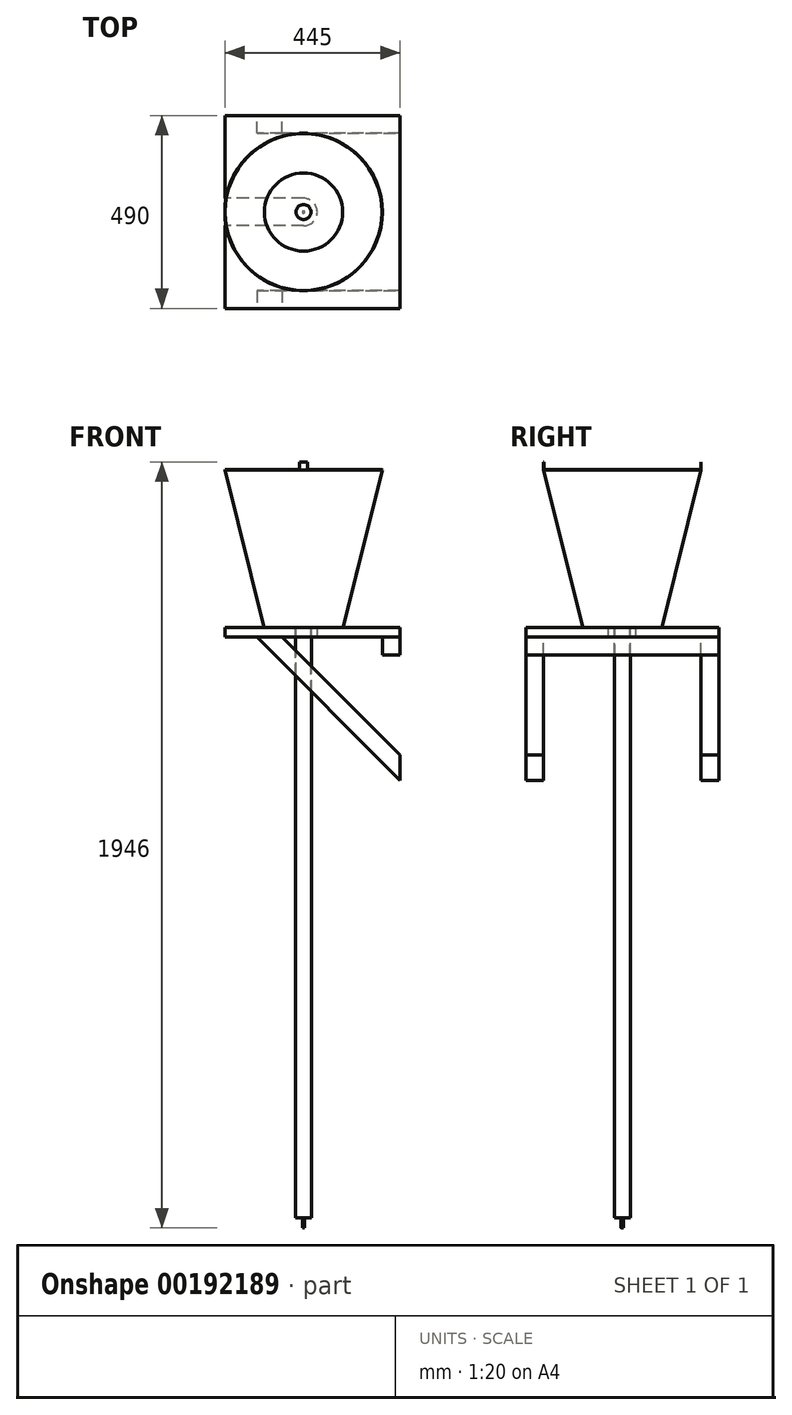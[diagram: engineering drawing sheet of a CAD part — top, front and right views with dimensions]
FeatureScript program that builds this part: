
annotation { "Feature Type Name" : "Feature", "Feature Type Description" : "" }
export const myFeature = defineFeature(function(context is Context, id is Id, definition is map)
    precondition{}
    {
        {
            assignVariable(context, id + "F0", {"name" : "BucketHeight", "anyValue" : 400});
        }
        {
            assignVariable(context, id + "F1", {"name" : "TubeThickness", "anyValue" : 1});
        }
        {
            assignVariable(context, id + "F2", {"name" : "TubeLength", "anyValue" : 1500});
        }
        {
            var Q0;
            Q0=qCreatedBy(makeId("Front.planeOp"),FACE);
            var sketch = newSketch(context, id + "F3", { "sketchPlane" : qUnion([Q0])});
            skLineSegment(sketch, "E0", {"start": v(-29.14, 0) * mm, "end": v(32.36, 0) * mm, "construction": true});
            skLineSegment(sketch, "E1", {"start": v(0, 36.8) * mm, "end": v(0, -14.35) * mm, "construction": true});
            skLineSegment(sketch, "E2", {"start": v(-200, 400) * mm, "end": v(-100, 0) * mm});
            skLineSegment(sketch, "E3", {"start": v(-100, 0) * mm, "end": v(0, 0) * mm});
            skLineSegment(sketch, "E4", {"start": v(0, 0) * mm, "end": v(0, 1) * mm});
            skLineSegment(sketch, "E5", {"start": v(0, 1) * mm, "end": v(-99.22, 1) * mm});
            skLineSegment(sketch, "E6", {"start": v(-99.22, 1) * mm, "end": v(-199.03, 400.24) * mm});
            skLineSegment(sketch, "E7", {"start": v(-199.03, 400.24) * mm, "end": v(-200, 400) * mm});
            skSolve(sketch);
        }
        {
            var Q0;
            Q0 = qSketchRegion(id + "F3", true);
            var Q1;
            Q1=sQuery(id+"F3.wireOp",EDGE,"E1");
            revolve(context, id + "F4", {"entities" : qUnion([Q0]), "axis" : qUnion([Q1]), "revolveType" : RevolveType.FULL});
        }
        {
            var Q0;
            Q0=qCreatedBy(makeId("Top.planeOp"),FACE);
            var sketch = newSketch(context, id + "F5", { "sketchPlane" : qUnion([Q0])});
            skCircle(sketch, "E8", {"center": v(0, 0) * mm, "radius": 20 * mm});
            skCircle(sketch, "E9", {"center": v(0, 0) * mm, "radius": 19 * mm});
            skSolve(sketch);
        }
        {
            var Q0;
            Q0 = qSketchRegion(id + "F5", true);
            extrude(context, id + "F6", {"entities" : qUnion([Q0]), "operationType" : NewBodyOperationType.ADD, "oppositeDirection" : true, "depth" : (getVariable(context, 'TubeLength')) * mm});
        }
        {
            var Q0;
            Q0=qCreatedBy(makeId("Top.planeOp"),FACE);
            var sketch = newSketch(context, id + "F7", { "sketchPlane" : qUnion([Q0])});
            skCircle(sketch, "E10", {"center": v(0, 0) * mm, "radius": 19 * mm});
            skSolve(sketch);
        }
        {
            var Q0;
            Q0 = qSketchRegion(id + "F7", true);
            extrude(context, id + "F8", {"entities" : qUnion([Q0]), "operationType" : NewBodyOperationType.REMOVE, "endBound" : BoundingType.THROUGH_ALL, "depth" : 25 * mm});
        }
        {
            var Q0;
            Q0=qCreatedBy(makeId("Top.planeOp"),FACE);
            cPlane(context, id + "F9", {"entities" : qUnion([Q0]), "cplaneType" : CPlaneType.OFFSET, "offset" : (getVariable(context, 'BucketHeight')) * mm, "width" : 150 * mm, "height" : 150 * mm});
        }
        {
            var Q0;
            Q0=qCreatedBy(id+"F9.planeOp",FACE);
            var sketch = newSketch(context, id + "F10", { "sketchPlane" : qUnion([Q0])});
            skLineSegment(sketch, "E11", {"start": v(0, -264.42) * mm, "end": v(0, 258.28) * mm, "construction": true});
            skLineSegment(sketch, "E12", {"start": v(-81.36, -200) * mm, "end": v(109.19, -200) * mm, "construction": true});
            skLineSegment(sketch, "E13", {"start": v(-77.86, -199.03) * mm, "end": v(90.54, -199.03) * mm, "construction": true});
            skLineSegment(sketch, "E14.bottom", {"start": v(-10, -200) * mm, "end": v(10, -200) * mm});
            skLineSegment(sketch, "E14.top", {"start": v(-10, -199.03) * mm, "end": v(10, -199.03) * mm});
            skLineSegment(sketch, "E14.left", {"start": v(-10, -200) * mm, "end": v(-10, -199.03) * mm});
            skLineSegment(sketch, "E14.right", {"start": v(10, -200) * mm, "end": v(10, -199.03) * mm});
            skLineSegment(sketch, "E15.MirrorCS", {"start": v(-10, 200) * mm, "end": v(-10, 199.03) * mm});
            skLineSegment(sketch, "E16.MirrorCS", {"start": v(10, 200) * mm, "end": v(10, 199.03) * mm});
            skLineSegment(sketch, "E17.MirrorCS", {"start": v(-10, 200) * mm, "end": v(10, 200) * mm});
            skLineSegment(sketch, "E18.MirrorCS", {"start": v(-10, 199.03) * mm, "end": v(10, 199.03) * mm});
            skSolve(sketch);
        }
        {
            var Q0;
            Q0 = qSketchRegion(id + "F10", true);
            extrude(context, id + "F11", {"entities" : qUnion([Q0]), "operationType" : NewBodyOperationType.ADD, "depth" : 20 * mm});
        }
        {
            var Q0;
            Q0=makeQuery(id+"F6.opExtrude","CAP_FACE",FACE,{"disambiguationData":[OSD([sQuery(id+"F5.wireOp",EDGE,"E8"),sQuery(id+"F5.wireOp",EDGE,"E9")])],"isStart":false});
            var sketch = newSketch(context, id + "F12", { "sketchPlane" : qUnion([Q0])});
            skCircle(sketch, "E19", {"center": v(0, 0) * mm, "radius": 20 * mm});
            skSolve(sketch);
        }
        {
            var Q0;
            Q0 = qSketchRegion(id + "F12", true);
            extrude(context, id + "F13", {"entities" : qUnion([Q0]), "operationType" : NewBodyOperationType.ADD, "depth" : (getVariable(context, 'TubeThickness')) * mm});
        }
        {
            var Q0;
            Q0=makeQuery(id+"F13.opExtrude","CAP_FACE",FACE,{"disambiguationData":[OSD([sQuery(id+"F12.wireOp",EDGE,"E19")])],"isStart":false});
            var sketch = newSketch(context, id + "F14", { "sketchPlane" : qUnion([Q0])});
            skCircle(sketch, "E20", {"center": v(0, 0) * mm, "radius": 3 * mm});
            skSolve(sketch);
        }
        {
            var Q0;
            Q0 = qSketchRegion(id + "F14", true);
            extrude(context, id + "F15", {"entities" : qUnion([Q0]), "depth" : 25 * mm});
        }
        {
            var Q0;
            Q0=qCreatedBy(makeId("Top.planeOp"),FACE);
            var sketch = newSketch(context, id + "F16", { "sketchPlane" : qUnion([Q0])});
            skLineSegment(sketch, "E21.bottom", {"start": v(245, -245) * mm, "end": v(-200, -245) * mm});
            skLineSegment(sketch, "E21.top", {"start": v(245, 245) * mm, "end": v(-200, 245) * mm});
            skLineSegment(sketch, "E21.left", {"start": v(245, -245) * mm, "end": v(245, 245) * mm});
            skLineSegment(sketch, "E21.right", {"start": v(-200, -245) * mm, "end": v(-200, -35) * mm});
            skLineSegment(sketch, "E22", {"start": v(347.7, 0) * mm, "end": v(-356.96, 0) * mm, "construction": true});
            skLineSegment(sketch, "E23", {"start": v(0, -400.86) * mm, "end": v(0, 467.96) * mm, "construction": true});
            skArc(sketch, "E24", {"start": v(0, -35) * mm, "mid": v(35, 0) * mm, "end": v(0, 35) * mm});
            skLineSegment(sketch, "E25", {"start": v(0, -35) * mm, "end": v(-200, -35) * mm});
            skLineSegment(sketch, "E26", {"start": v(-200, -35) * mm, "end": v(-191.36, -29) * mm});
            skLineSegment(sketch, "E27", {"start": v(0, 35) * mm, "end": v(-200, 35) * mm});
            skLineSegment(sketch, "E28.trimOffspring", {"start": v(-200, 35) * mm, "end": v(-200, 245) * mm});
            skSolve(sketch);
        }
        {
            var Q0;
            Q0 = qSketchRegion(id + "F16", true);
            extrude(context, id + "F17", {"entities" : qUnion([Q0]), "operationType" : NewBodyOperationType.ADD, "oppositeDirection" : true, "depth" : 25 * mm});
        }
        {
            var Q0;
            Q0=makeQuery(id+"F17.opExtrude","CAP_FACE",FACE,{"disambiguationData":[OSD([sQuery(id+"F16.wireOp",EDGE,"E21.bottom"),sQuery(id+"F16.wireOp",EDGE,"E21.top"),sQuery(id+"F16.wireOp",EDGE,"E21.left"),sQuery(id+"F16.wireOp",EDGE,"E21.right"),sQuery(id+"F16.wireOp",EDGE,"E24"),sQuery(id+"F16.wireOp",EDGE,"E25"),sQuery(id+"F16.wireOp",EDGE,"E27"),sQuery(id+"F16.wireOp",EDGE,"E28.trimOffspring")])],"isStart":false});
            var sketch = newSketch(context, id + "F18", { "sketchPlane" : qUnion([Q0])});
            skLineSegment(sketch, "E29.bottom", {"start": v(245, -245) * mm, "end": v(200, -245) * mm});
            skLineSegment(sketch, "E29.top", {"start": v(245, 245) * mm, "end": v(200, 245) * mm});
            skLineSegment(sketch, "E29.left", {"start": v(245, -245) * mm, "end": v(245, 245) * mm});
            skLineSegment(sketch, "E29.right", {"start": v(200, -245) * mm, "end": v(200, 245) * mm});
            skSolve(sketch);
        }
        {
            var Q0;
            Q0 = qSketchRegion(id + "F18", true);
            extrude(context, id + "F19", {"entities" : qUnion([Q0]), "depth" : 45 * mm});
        }
        {
            var Q0;
            Q0=makeQuery(id+"F17.opExtrude","SWEPT_FACE",FACE,{"disambiguationData":[OSD([sQuery(id+"F16.wireOp",EDGE,"E21.bottom")])]});
            var sketch = newSketch(context, id + "F20", { "sketchPlane" : qUnion([Q0])});
            skLineSegment(sketch, "E30", {"start": v(-118.64, -25) * mm, "end": v(245, -388.64) * mm});
            skLineSegment(sketch, "E31", {"start": v(245, -388.64) * mm, "end": v(245, -325) * mm});
            skLineSegment(sketch, "E32", {"start": v(245, -325) * mm, "end": v(-55, -25) * mm});
            skLineSegment(sketch, "E33", {"start": v(-55, -25) * mm, "end": v(-118.64, -25) * mm});
            skLineSegment(sketch, "E34", {"start": v(245, 156.79) * mm, "end": v(245, -393.67) * mm, "construction": true});
            skSolve(sketch);
        }
        {
            var Q0;
            Q0 = qSketchRegion(id + "F20", true);
            extrude(context, id + "F21", {"entities" : qUnion([Q0]), "oppositeDirection" : true, "depth" : 45 * mm});
        }
        {
            var Q0;
            Q0=makeQuery(id+"F21.opExtrude","SWEPT_BODY",BODY,{"disambiguationData":[OSD([sQuery(id+"F20.wireOp",EDGE,"E30"),sQuery(id+"F20.wireOp",EDGE,"E31"),sQuery(id+"F20.wireOp",EDGE,"E32"),sQuery(id+"F20.wireOp",EDGE,"E33")])]});
            var Q1;
            Q1=qCreatedBy(makeId("Front.planeOp"),FACE);
            mirror(context, id + "F22", {"entities" : qUnion([Q0]), "mirrorPlane" : qUnion([Q1])});
        }
    });
